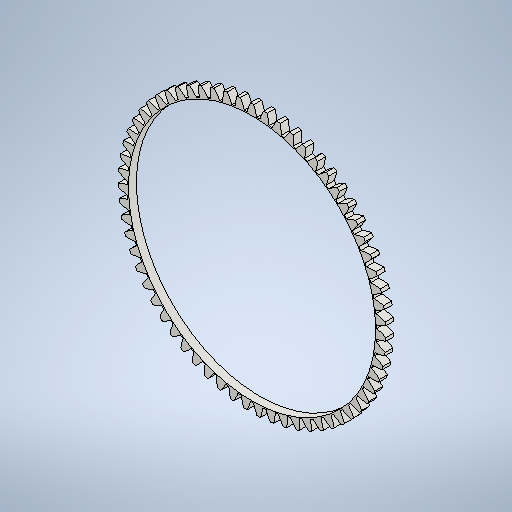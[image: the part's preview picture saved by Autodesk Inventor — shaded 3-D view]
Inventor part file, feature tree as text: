
AUTODESK INVENTOR PART (.ipt)
format: ipt  version: 2025.3 (Build 293356030, 356C)  size: 1,230,848 bytes
history: native  units: mm (DEFAULTED — no unit token found)
features: extrude x4, other x4, sketch x4, plane x3, projected_geometry x2, pattern_circular x1, fillet x1
ambient origin geometry x8: Origin, YZ Plane, XZ Plane, XY Plane, X Axis, Y Axis, Z Axis, Center Point
bodies: Solid1 (feature_tree)
feature tree (19):
  extrude  "Extrusion1"  Depth=24.0mm TaperAngle=0.0deg
  plane  "Work Plane2"
  plane  "Work Plane8"
  plane  "Work Plane9"
  other  "Spur Gear"
  extrude  "Extrusion2"  Depth=10.0mm TaperAngle=0.0deg
  extrude  "Extrusion3"  Depth=0.498666mm TaperAngle=0.0deg
  pattern_circular  "Circular Pattern1"  [2 undecoded]
  fillet  "Fillet1"  Radius=494.0mm
  extrude  "Extrusion4"  Depth=494.0mm
  sketch  "Sketch1"  dims[d0=812.91152mm d1=24.0mm d2=0.0mm]
  other  "Srf1"
  sketch  "Sketch3"  dims[d3=787.89816mm d4=10.0mm d5=0.0mm]
  projected_geometry  "Projected Loop1"
  sketch  "Sketch4"  dims[d16=494.0mm d17=0.0mm d34=0.498666mm]
  sketch  "Sketch5"  dims[d39=0.0mm d41=0.0mm d43=494.0mm d46=494.0mm d47=0.0mm d48=0.0mm d49=250.0mm d50=0.0mm d51=0.0mm d52=12.5mm d53=145.0mm d54=0.0mm d55=0.0mm d56=80.0mm d57=360.0deg d59=1.0mm d60=750.0mm d61=0.0mm d62=0.0mm]
  projected_geometry  "Projected Loop2"
  other  "Pitch Diameter"
  other  "Definition1"
note: 2 required parameter values undecoded (feature->parameter linkage not recoverable at this tier; creation-order binding heuristic only, values carry confidence <= 0.55)
